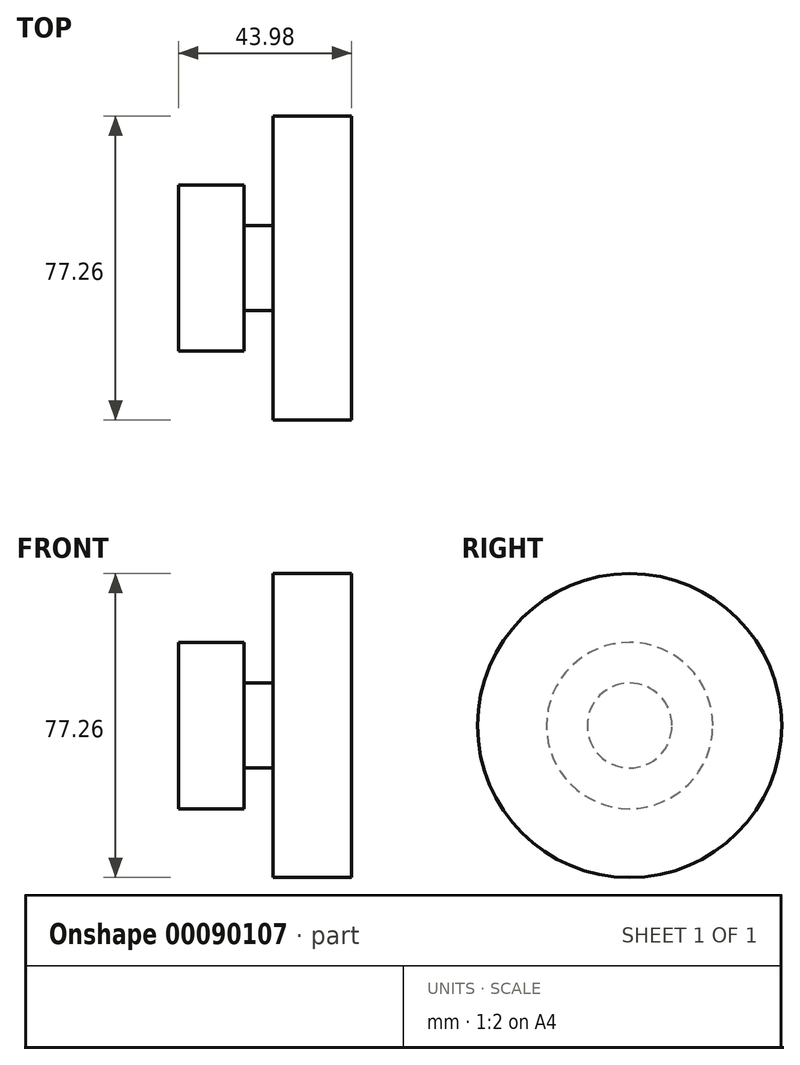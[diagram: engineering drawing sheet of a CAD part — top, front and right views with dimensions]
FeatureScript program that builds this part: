
annotation { "Feature Type Name" : "Feature", "Feature Type Description" : "" }
export const myFeature = defineFeature(function(context is Context, id is Id, definition is map)
    precondition{}
    {
        {
            var Q0;
            Q0=qCreatedBy(makeId("Top.planeOp"),FACE);
            var sketch = newSketch(context, id + "F0", { "sketchPlane" : qUnion([Q0])});
            skLineSegment(sketch, "E0", {"start": v(-31.81, 0) * mm, "end": v(-31.81, 21.12) * mm});
            skLineSegment(sketch, "E1", {"start": v(-31.81, 21.12) * mm, "end": v(-15.13, 21.12) * mm});
            skLineSegment(sketch, "E2", {"start": v(-15.13, 21.12) * mm, "end": v(-15.13, 10.78) * mm});
            skLineSegment(sketch, "E3", {"start": v(-15.13, 10.78) * mm, "end": v(-7.82, 10.78) * mm});
            skLineSegment(sketch, "E4", {"start": v(-7.82, 10.78) * mm, "end": v(-7.82, 38.63) * mm});
            skLineSegment(sketch, "E5", {"start": v(-7.82, 38.63) * mm, "end": v(12.17, 38.63) * mm});
            skLineSegment(sketch, "E6", {"start": v(12.17, 38.63) * mm, "end": v(12.17, 0) * mm});
            skLineSegment(sketch, "E7", {"start": v(12.17, 0) * mm, "end": v(-31.81, 0) * mm});
            skSolve(sketch);
        }
        {
            var Q0;
            Q0 = qSketchRegion(id + "F0", true);
            var Q1;
            Q1=sQuery(id+"F0.wireOp",EDGE,"E7");
            revolve(context, id + "F1", {"entities" : qUnion([Q0]), "axis" : qUnion([Q1]), "revolveType" : RevolveType.FULL});
        }
    });
